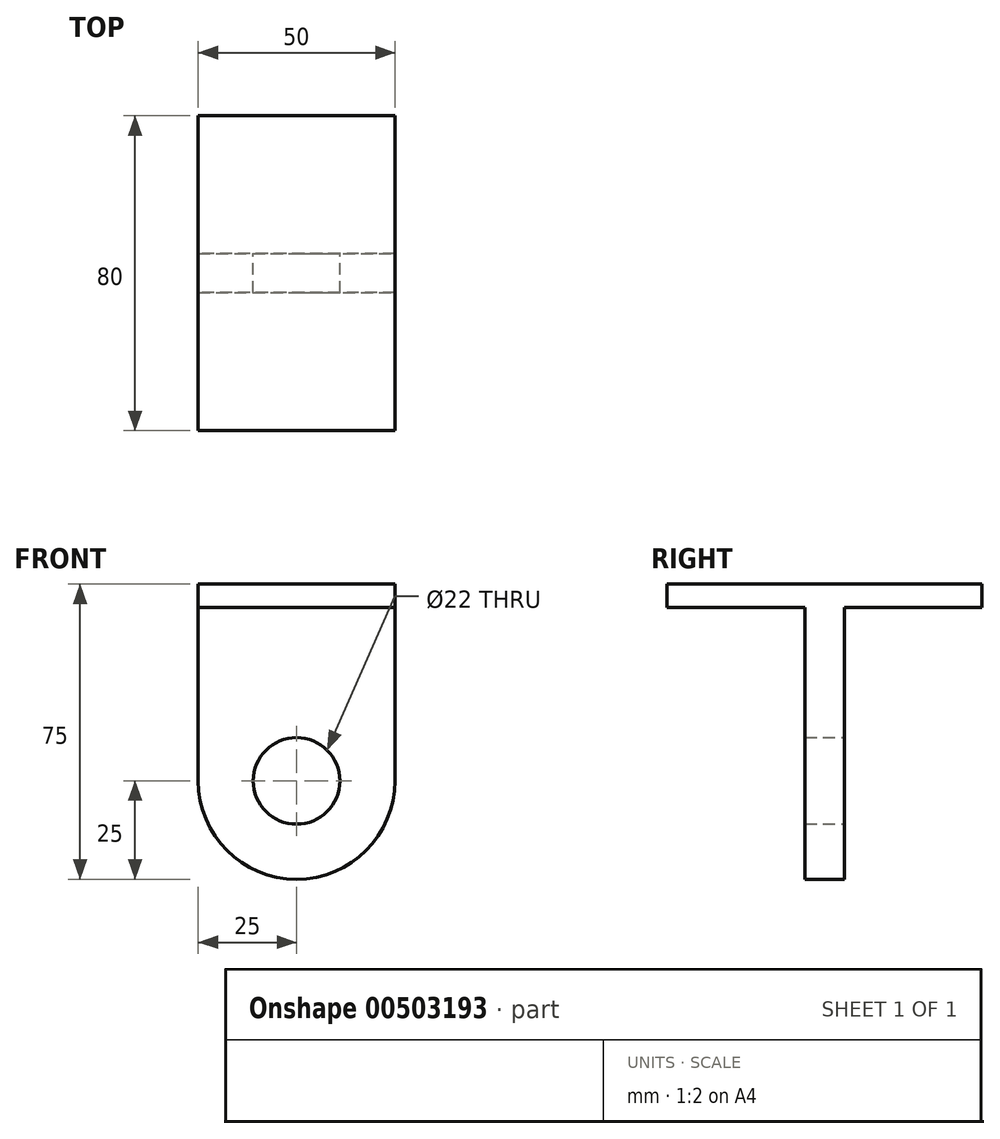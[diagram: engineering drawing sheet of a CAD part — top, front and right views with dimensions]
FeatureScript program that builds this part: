
annotation { "Feature Type Name" : "Feature", "Feature Type Description" : "" }
export const myFeature = defineFeature(function(context is Context, id is Id, definition is map)
    precondition{}
    {
        {
            var Q0;
            Q0=qCreatedBy(makeId("Front.planeOp"),FACE);
            var sketch = newSketch(context, id + "F0", { "sketchPlane" : qUnion([Q0])});
            skCircle(sketch, "E0", {"center": v(0, 0) * mm, "radius": 11 * mm});
            skArc(sketch, "E1", {"start": v(-25, 0) * mm, "mid": v(0, -25) * mm, "end": v(25, 0) * mm});
            skLineSegment(sketch, "E2", {"start": v(-25, 0) * mm, "end": v(-25, 50) * mm});
            skLineSegment(sketch, "E3", {"start": v(-25, 50) * mm, "end": v(25, 50) * mm});
            skLineSegment(sketch, "E4", {"start": v(25, 50) * mm, "end": v(25, 0) * mm});
            skLineSegment(sketch, "E5", {"start": v(-25, 44) * mm, "end": v(25, 44) * mm});
            skSolve(sketch);
        }
        {
            var Q0;
            Q0=makeQuery(id+"F0.imprint","IMPRINT",FACE,{"disambiguationData":[TD([[makeQuery(id+"F0.imprint","IMPRINT",EDGE,{"derivedFrom":sQuery(id+"F0.wireOp",EDGE,"E0")}),-1.0]])]});
            var Q1;
            {var subQ0=sQuery(id+"F0.wireOp",EDGE,"E3");Q1=makeQuery(id+"F0.imprint","IMPRINT",FACE,{"disambiguationData":[TD([[makeQuery(id+"F0.imprint","IMPRINT",EDGE,{"derivedFrom":subQ0}),-1.0]])]});}
            extrude(context, id + "F1", {"entities" : qUnion([Q0, Q1]), "endBound" : BoundingType.SYMMETRIC, "depth" : 10 * mm});
        }
        {
            var Q0;
            {var subQ0=sQuery(id+"F0.wireOp",EDGE,"E3");Q0=makeQuery(id+"F0.imprint","IMPRINT",FACE,{"disambiguationData":[TD([[makeQuery(id+"F0.imprint","IMPRINT",EDGE,{"derivedFrom":subQ0}),-1.0]])]});}
            extrude(context, id + "F2", {"entities" : qUnion([Q0]), "operationType" : NewBodyOperationType.ADD, "endBound" : BoundingType.SYMMETRIC, "depth" : 80 * mm});
        }
    });
